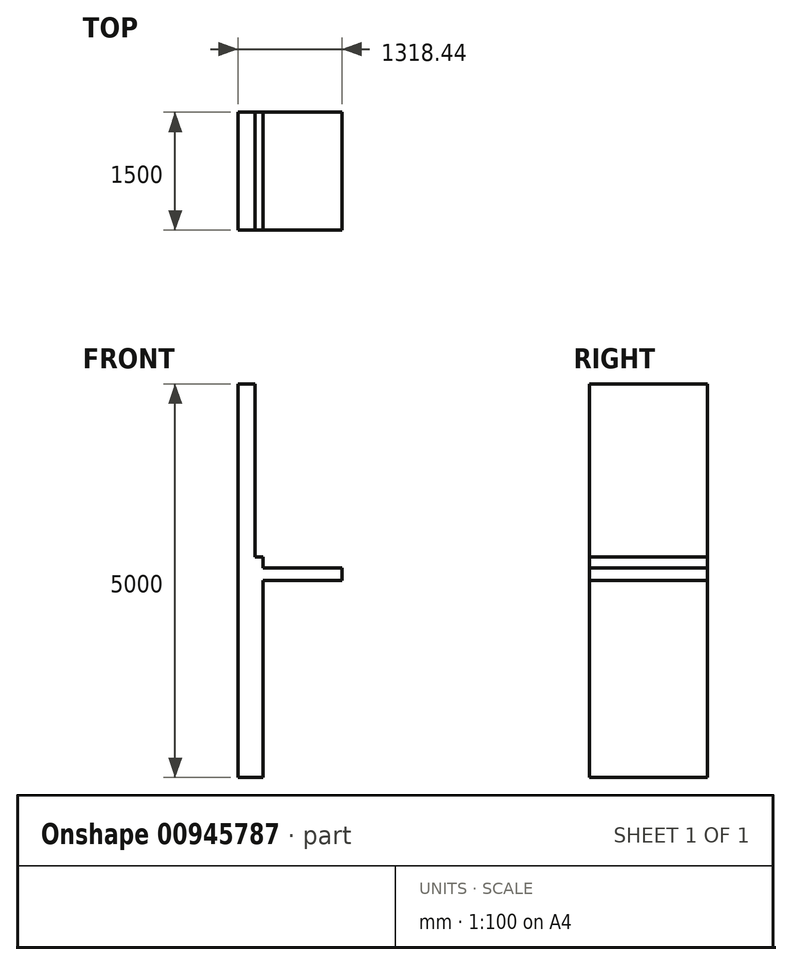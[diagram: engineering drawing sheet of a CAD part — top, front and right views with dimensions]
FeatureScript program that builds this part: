
annotation { "Feature Type Name" : "Feature", "Feature Type Description" : "" }
export const myFeature = defineFeature(function(context is Context, id is Id, definition is map)
    precondition{}
    {
        {
            var Q0;
            Q0=qCreatedBy(makeId("Front.planeOp"),FACE);
            var sketch = newSketch(context, id + "F0", { "sketchPlane" : qUnion([Q0])});
            skLineSegment(sketch, "E0.bottom", {"start": v(-95.13, 2204.37) * mm, "end": v(904.87, 2204.37) * mm});
            skLineSegment(sketch, "E0.top", {"start": v(-95.13, 2044.37) * mm, "end": v(904.87, 2044.37) * mm});
            skLineSegment(sketch, "E0.right", {"start": v(904.87, 2204.37) * mm, "end": v(904.87, 2044.37) * mm});
            skLineSegment(sketch, "E1.bottom", {"start": v(-95.13, -455.63) * mm, "end": v(-413.57, -455.63) * mm});
            skLineSegment(sketch, "E1.top", {"start": v(-95.13, 2344.37) * mm, "end": v(-201.3, 2344.37) * mm});
            skLineSegment(sketch, "E1.right", {"start": v(-413.57, -455.63) * mm, "end": v(-413.57, 2344.37) * mm});
            skLineSegment(sketch, "E2.top", {"start": v(-413.57, 4544.37) * mm, "end": v(-201.3, 4544.37) * mm});
            skLineSegment(sketch, "E2.left", {"start": v(-413.57, 2344.37) * mm, "end": v(-413.57, 4544.37) * mm});
            skLineSegment(sketch, "E2.right", {"start": v(-201.3, 2344.37) * mm, "end": v(-201.3, 4544.37) * mm});
            skLineSegment(sketch, "E3.trimOffspring", {"start": v(-95.13, 2204.37) * mm, "end": v(-95.13, 2344.37) * mm});
            skLineSegment(sketch, "E4", {"start": v(-95.13, 2044.37) * mm, "end": v(-95.13, -455.63) * mm});
            skSolve(sketch);
        }
        {
            var Q0;
            Q0 = qSketchRegion(id + "F0", true);
            extrude(context, id + "F1", {"entities" : qUnion([Q0]), "depth" : 1500 * mm, "offsetDistance" : 25 * mm});
        }
    });
